# Revit family: IS_CeramixBlue_B9490_BIM_DE
name_source: partatom
category: Plumbing Fixtures
revit_build: Autodesk Revit MEP 2016 (Build: 20161004_0715(x64)
units: mm (PartAtom-declared; Revit-internal decimal feet)

## family parameters
Always vertical = No
Cut with Voids When Loaded = No
OmniClass Number = 23.45.55.17
OmniClass Title = Mixing Faucets
Part Type = Normal
Room Calculation Point = No
Round Connector Dimension = Use Diameter
Shared = No
Work Plane-Based = No

## types (1)
- B9490AA CERAMIX BLUE exposed bath shower single lever mixer
    Accessories = www.idealstandard.de\ersatzteile
    AssetType = Fixed
    BIMObjectName = ISI_IdealStandard_BathTaps_CERAMIXBLUE_B9490AA
    BIMobject category = Taps & Mixers
    BOSUseNativeGeometries = 1
    BarCode = 3800861022114
    Brand = Ideal Standard
    Brand url = http://www.idealstandard.de
    CodePerformance = 0
    Color = Chrome
    ConnectionType = Plumbing
    Cost = 0 $
    CurrencyUnit = €
    CurrentRevision = 1
    Description = B9490AA CERAMIX BLUE exposed bath shower single lever mixer
    DurationUnit = Jaar
    EAN code = https://3800861022114
    Edition number = 1
    ExpectedLife = 25
    FaucetFunction = mixed
    FaucetOperation = leverhandle
    FaucetType = pillar
    Features = CERAMIX BLUE exposed bath shower single lever mixer
    Finish = Chrome
    IFC Classification = Sanitary Terminal
    IfcExportAs = Sanitary terminal type
    IfcExportType = BRASSWARE BATH
    Installation instructions = http://www.idealstandard.de
    InstallationInstructions = www.idealstandard.de\produkte
    LinearUnits = millimetres
    MainColor = Chrome
    MaintenanceInformation = www.idealstandard.de
    Manufacturer = http://www.idealstandard.de
    Manufacturer name = Ideal Standard
    ManufacturerURL = http://www.idealstandard.de
    Material = Brass
    Material main = Brass
    Model = B9490AA
    ModelNumber = B9490AA
    ModelReference = B9490AA CERAMIX BLUE exposed bath shower single lever mixer
    NBS Reference Code = 35-06-07
    NBS Reference Description = Bath Water Supply Fittings
    Name = ISI_IdealStandard_BathTaps_CERAMIXBLUE_B9490AA
    NettWeight = 2,331 kg
    Nominal height = 0
    Nominal width = 0
    NominalHeight = 122 mm
    NominalLength = 199 mm
    NominalWidth = 220 mm
    OmniClass Code = 23-31 11 00
    OmniClass Description = Faucets
    Product Guid = 3c07279f-5cd0-4d31-a7c0-a0232d057bc6
    Product SKU = B9490
    Product certification = 0
    Product data url = https://bimobject.com
    Product family = CERAMIX BLUE
    Product group = Bath & Shower Mixer
    Product name = CERAMIX BLUE exposed bath shower single lever mixer
    Product url = http://www.idealstandard.de
    ProductInformation = www.idealstandard.de/produkte
    QR code = http://bimobject.com
    Shape = Sculptured
    Size = 220x199x122 mm
    Space = Internal
    SpareParts = www.idealstandard.de/ersatzteile
    Technical description = http://www.idealstandard.de
    TestPressure = 10 Bar
    URL = http://www.idealstandard.de
    Uniclass 1.4 Code = L8212
    Uniclass 1.4 Description = Fittings
    Uniclass 2.0 Code = PR-35-06-07
    Uniclass 2.0 Description = Bath Water Supply Fittings
    Uniclass 2015 Code = Pr_40_20_87_07
    Uniclass 2015 Name = Bath manual water supply sets
    Uniclass2015Code = Pr_40_20_87_09
    Uniclass2015Title = Bath taps
    Uniclass2015Version = Products v1.1
    ValveMechanism = ceramic disc
    ValveOperation = lever
    VolumeUnits = Litres
    Weight Net (Kg) = 2.33
    WorkingPressure = 1-5 Bar

## geometry (parser evidence)
native form markers: Blend x4, Sweep x1
no freeform markers — native parametric forms only
